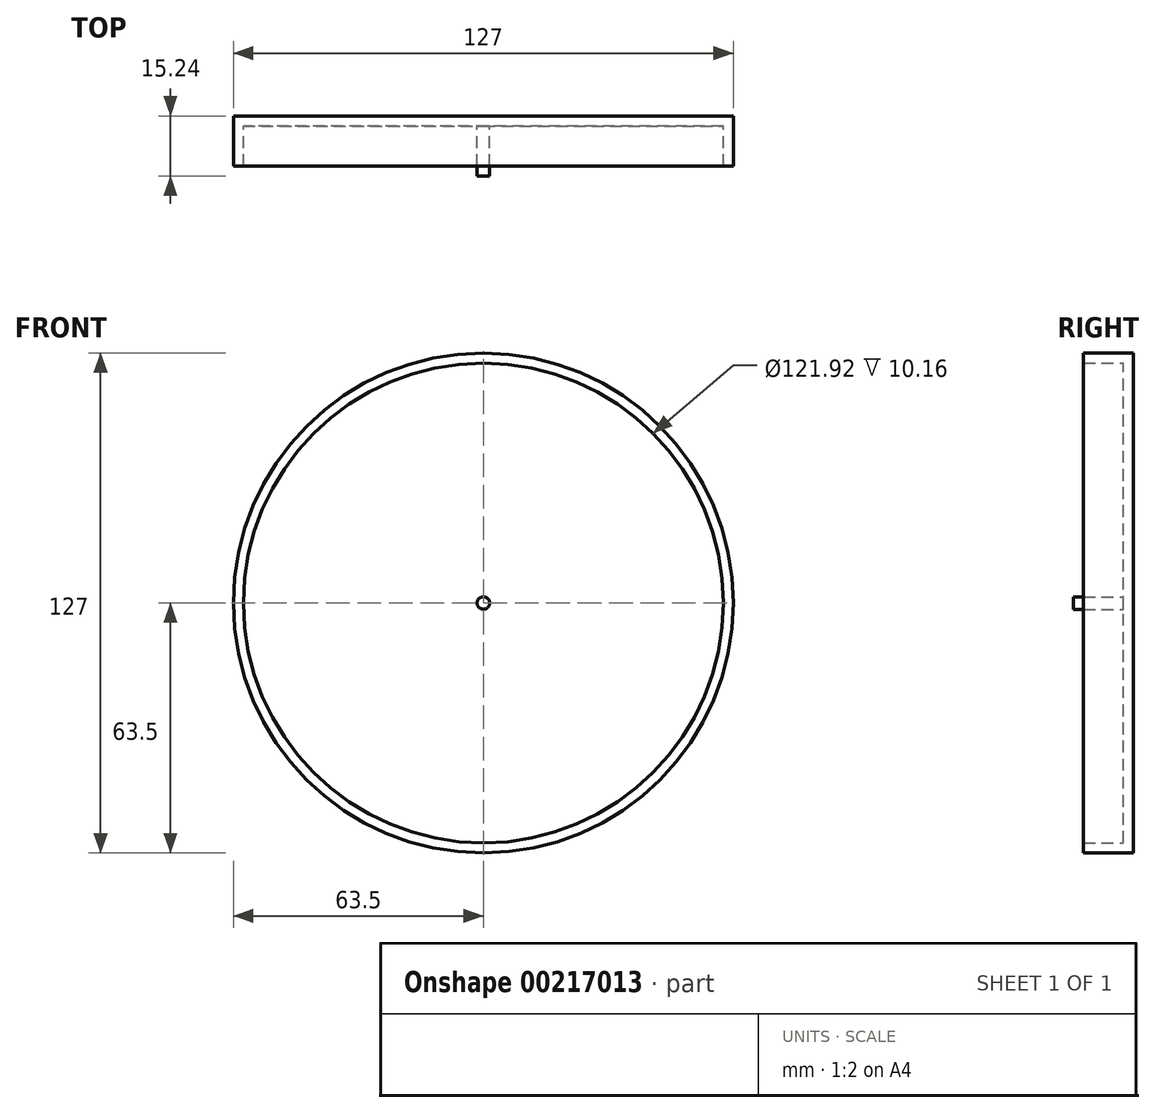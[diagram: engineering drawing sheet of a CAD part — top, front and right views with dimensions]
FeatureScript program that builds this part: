
annotation { "Feature Type Name" : "Feature", "Feature Type Description" : "" }
export const myFeature = defineFeature(function(context is Context, id is Id, definition is map)
    precondition{}
    {
        {
            var Q0;
            Q0=qCreatedBy(makeId("Front.planeOp"),FACE);
            var sketch = newSketch(context, id + "F0", { "sketchPlane" : qUnion([Q0])});
            skCircle(sketch, "E0", {"center": v(0, 0) * mm, "radius": 63.5 * mm});
            skSolve(sketch);
        }
        {
            var Q0;
            Q0=makeQuery(id+"F0.imprint","IMPRINT",FACE,{"disambiguationData":[TD([[makeQuery(id+"F0.imprint","IMPRINT",EDGE,{"derivedFrom":sQuery(id+"F0.wireOp",EDGE,"E0")}),1.0]])]});
            extrude(context, id + "F1", {"entities" : qUnion([Q0]), "depth" : 12.7 * mm});
        }
        {
            var Q0;
            Q0=makeQuery(id+"F1.opExtrude","CAP_FACE",FACE,{"disambiguationData":[OSD([sQuery(id+"F0.wireOp",EDGE,"E0")])],"isStart":false});
            shell(context, id + "F2", {"entities" : qUnion([Q0]), "thickness" : 2.54 * mm});
        }
        {
            var Q0;
            {var subQ0=sQuery(id+"F0.wireOp",EDGE,"E0");Q0=makeQuery(id+"F2.opShell","OFFSET_FACE",FACE,{"disambiguationData":[OSD([subQ0]),TDD([makeQuery(id+"F1.opExtrude","CAP_FACE",FACE,{"disambiguationData":[OSD([subQ0])],"isStart":true})])]});}
            var sketch = newSketch(context, id + "F3", { "sketchPlane" : qUnion([Q0])});
            skCircle(sketch, "E1", {"center": v(0, 0) * mm, "radius": 1.59 * mm});
            skSolve(sketch);
        }
        {
            var Q0;
            Q0=makeQuery(id+"F3.imprint","IMPRINT",FACE,{"disambiguationData":[TD([[makeQuery(id+"F3.imprint","IMPRINT",EDGE,{"derivedFrom":sQuery(id+"F3.wireOp",EDGE,"E1")}),1.0]])]});
            extrude(context, id + "F4", {"entities" : qUnion([Q0]), "operationType" : NewBodyOperationType.ADD, "depth" : 12.7 * mm});
        }
    });
